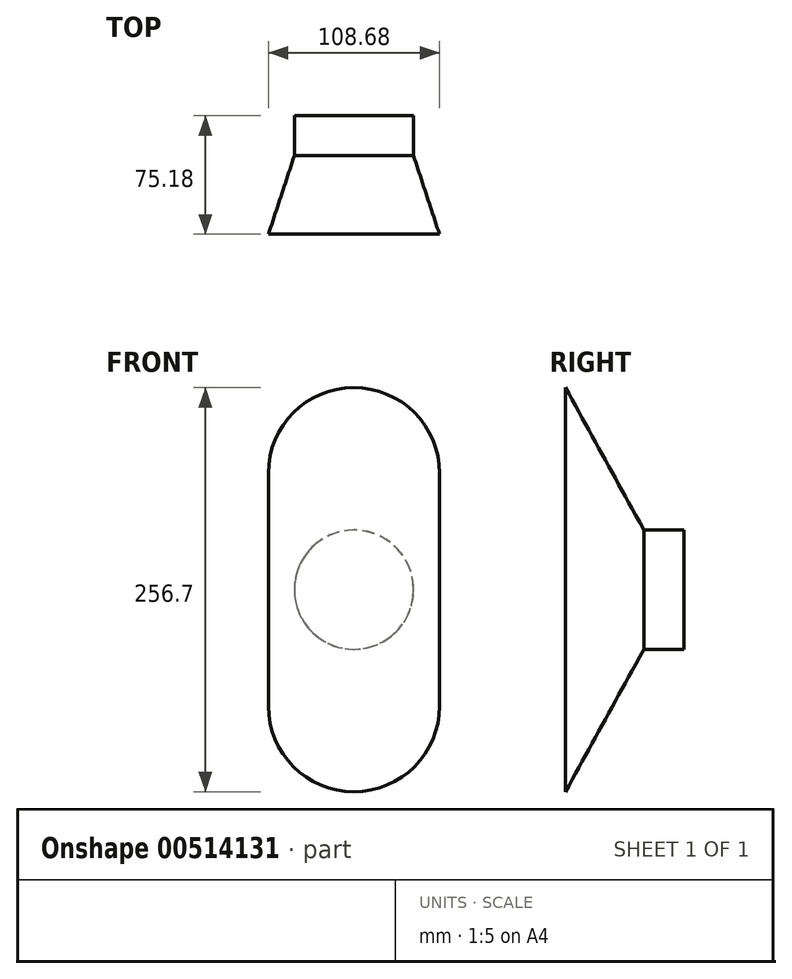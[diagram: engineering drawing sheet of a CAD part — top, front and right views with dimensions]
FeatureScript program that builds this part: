
annotation { "Feature Type Name" : "Feature", "Feature Type Description" : "" }
export const myFeature = defineFeature(function(context is Context, id is Id, definition is map)
    precondition{}
    {
        {
            var Q0;
            Q0=qCreatedBy(makeId("Front.planeOp"),FACE);
            var sketch = newSketch(context, id + "F0", { "sketchPlane" : qUnion([Q0])});
            skCircle(sketch, "E0", {"center": v(0, 0) * mm, "radius": 37.85 * mm});
            skSolve(sketch);
        }
        {
            var Q0;
            Q0=qCreatedBy(makeId("Front.planeOp"),FACE);
            cPlane(context, id + "F1", {"entities" : qUnion([Q0]), "cplaneType" : CPlaneType.OFFSET, "offset" : 62.48 * mm, "width" : 152.4 * mm, "height" : 152.4 * mm});
        }
        {
            var Q0;
            Q0=qCreatedBy(id+"F1.planeOp",FACE);
            var sketch = newSketch(context, id + "F2", { "sketchPlane" : qUnion([Q0])});
            skLineSegment(sketch, "E1.bottom", {"start": v(54.34, -74.01) * mm, "end": v(-54.34, -74.01) * mm, "construction": true});
            skLineSegment(sketch, "E1.top", {"start": v(54.34, 74.01) * mm, "end": v(-54.34, 74.01) * mm, "construction": true});
            skLineSegment(sketch, "E1.left", {"start": v(54.34, -74.01) * mm, "end": v(54.34, 74.01) * mm});
            skLineSegment(sketch, "E1.right", {"start": v(-54.34, -74.01) * mm, "end": v(-54.34, 74.01) * mm});
            skPoint(sketch, "E1.middle", {"position": v(0, 0) * mm});
            skArc(sketch, "E2", {"start": v(54.34, 74.01) * mm, "mid": v(0, 128.35) * mm, "end": v(-54.34, 74.01) * mm});
            skArc(sketch, "E3", {"start": v(-54.34, -74.01) * mm, "mid": v(0, -128.35) * mm, "end": v(54.34, -74.01) * mm});
            skSolve(sketch);
        }
        {
            var Q0;
            Q0=makeQuery(id+"F0.imprint","IMPRINT",FACE,{"disambiguationData":[TD([[makeQuery(id+"F0.imprint","IMPRINT",EDGE,{"derivedFrom":sQuery(id+"F0.wireOp",EDGE,"E0")}),1.0]])]});
            extrude(context, id + "F3", {"entities" : qUnion([Q0]), "endBound" : BoundingType.SYMMETRIC, "depth" : 25.4 * mm});
        }
        {
            var Q0;
            Q0=makeQuery(id+"F3.opExtrude","CAP_FACE",FACE,{"disambiguationData":[OSD([sQuery(id+"F0.wireOp",EDGE,"E0")])],"isStart":false});
            var sketch = newSketch(context, id + "F4", { "sketchPlane" : qUnion([Q0])});
            skArc(sketch, "E4", {"start": v(-23.34, 29.8) * mm, "mid": v(-37.85, 0.62) * mm, "end": v(-24.3, -29.02) * mm});
            skLineSegment(sketch, "E5", {"start": v(22.87, 30.16) * mm, "end": v(22.87, 30.16) * mm});
            skArc(sketch, "E6", {"start": v(22.87, 30.16) * mm, "mid": v(-0.3, 37.85) * mm, "end": v(-23.34, 29.8) * mm});
            skArc(sketch, "E7", {"start": v(23.9, -29.36) * mm, "mid": v(37.85, 0.65) * mm, "end": v(22.87, 30.16) * mm});
            skArc(sketch, "E8", {"start": v(-24.3, -29.02) * mm, "mid": v(-0.26, -37.85) * mm, "end": v(23.9, -29.36) * mm});
            skSolve(sketch);
        }
        {
            var Q0;
            Q0 = qSketchRegion(id + "F4", true);
            var Q1;
            Q1 = qSketchRegion(id + "F2", true);
            loft(context, id + "F5", {"sheetProfilesArray" : [{ "sheetProfileEntities" : qUnion([Q0]) }, { "sheetProfileEntities" : qUnion([Q1]) }]});
        }
    });
